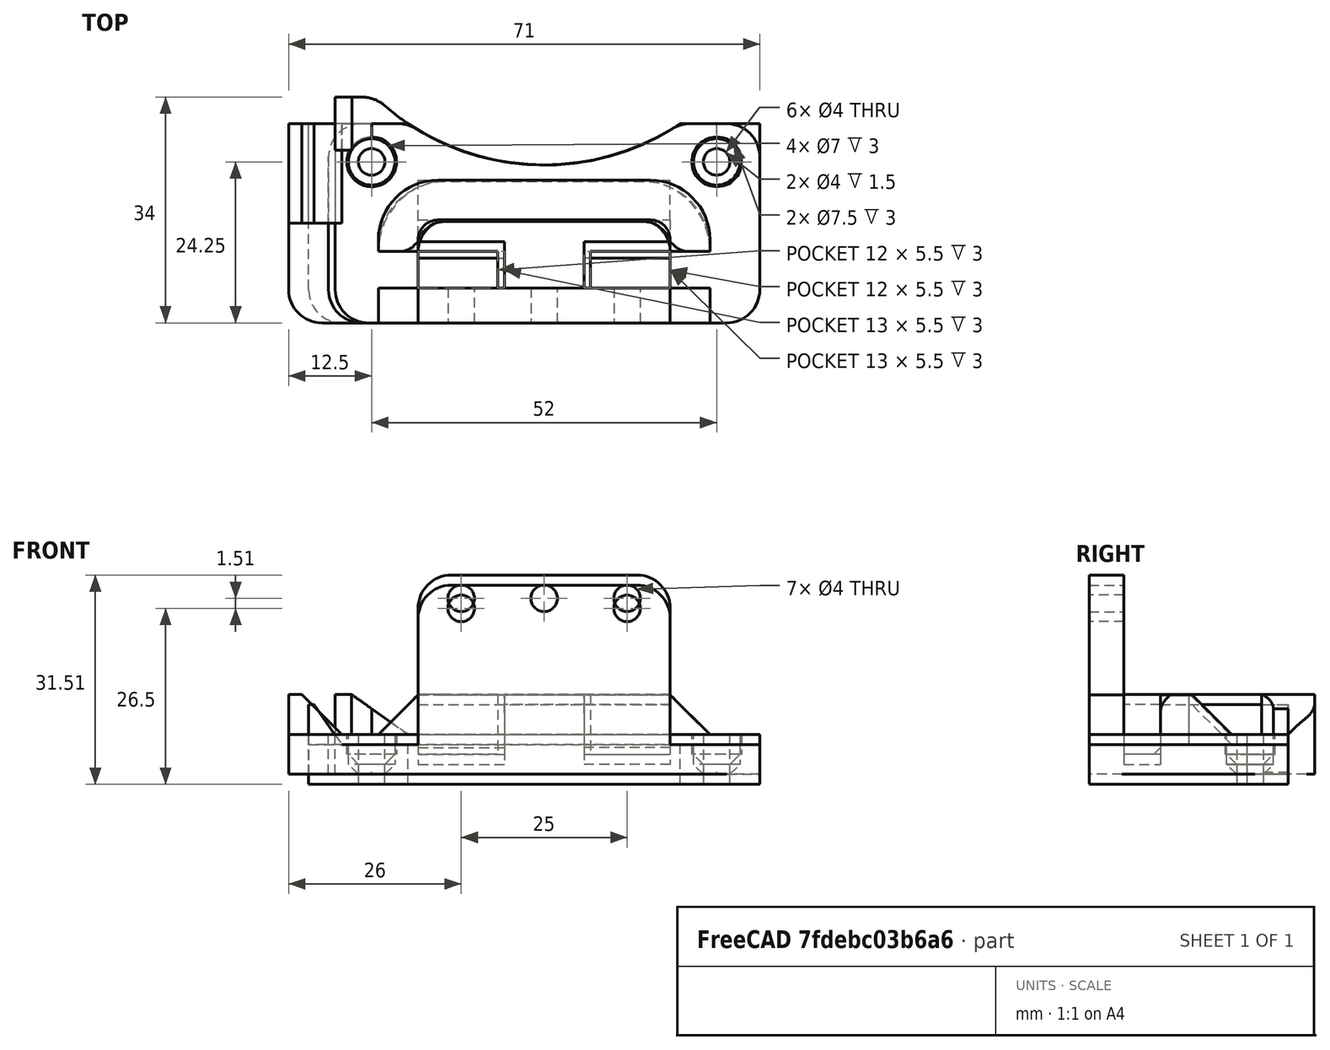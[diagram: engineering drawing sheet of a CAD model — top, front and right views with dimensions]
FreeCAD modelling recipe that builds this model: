
FCSTD DOCUMENT  (FreeCAD 0.18R4 (GitTag))
Label: y_belt_mount_v0.3
License: CreativeCommons Attribution-ShareAlike
LicenseURL: http://creativecommons.org/licenses/by-sa/4.0/
objects: Sketcher::SketchObject×7, PartDesign::Pocket×6, PartDesign::Fillet×3, PartDesign::Chamfer×3, Part::FeaturePython×2, App::FeaturePython×2, PartDesign::Pad×1, PartDesign::Body×1
note: 30 computed .brp shape members not serialized (recipe doc carries the construction recipe); baked Part::Feature solids carry a one-line shape summary decoded from their .brp

FEATURE [Sketcher::SketchObject] Sketch
  MapMode = 5
  Support = -> [XY_Plane]
  sketch-geometry (9):
    g0: LineSegment StartX=64 StartY=0 StartZ=0 EndX=64 EndY=30 EndZ=0
    g1: LineSegment StartX=64 StartY=30 StartZ=0 EndX=52 EndY=30 EndZ=0
    g2: LineSegment StartX=0 StartY=34 StartZ=0 EndX=0 EndY=0 EndZ=0
    g3: LineSegment StartX=0 StartY=0 StartZ=0 EndX=64 EndY=0 EndZ=0
    g4: ArcOfCircle CenterX=31.5 CenterY=60.5 CenterZ=0 NormalX=0 NormalY=0 NormalZ=1 AngleXU=0 Radius=36.7491 StartAngle=3.94699 EndAngle=5.30417
    g5: Circle CenterX=5.5 CenterY=24.25 CenterZ=0 NormalX=0 NormalY=0 NormalZ=1 AngleXU=0 Radius=2
    g6: Circle CenterX=57.5 CenterY=24.25 CenterZ=0 NormalX=0 NormalY=0 NormalZ=1 AngleXU=0 Radius=2
    g7: LineSegment [constr] StartX=5.5 StartY=24.25 StartZ=0 EndX=57.5 EndY=24.25 EndZ=0
    g8: LineSegment StartX=0 StartY=34 StartZ=0 EndX=6.03925 EndY=34 EndZ=0
  constraints (26):
    c: Coincident(g0,g1)
    c: Coincident(g2,g3)
    c: Coincident(g0,g3)
    c: Coincident(g2,g-1)
    c: Vertical(g2)
    c: Vertical(g0)
    c: Horizontal(g3)
    c: Horizontal(g1)
    c: DistanceX(g3,g3) = 64
    c: DistanceX(g1,g1) = 12
    c: Coincident(g1,g4)
    c: DistanceY(g0,g0) = 30
    c: DistanceX(g5) = 5.5
    c: DistanceY(g5) = 24.25
    c: Coincident(g6,g7)
    c: Coincident(g5,g7)
    c: Horizontal(g7)
    c: DistanceX(g7,g7) = 52
    c: Equal(g5,g6)
    c: Radius(g6) = 2
    c: DistanceX(g4) = 31.5
    c: DistanceY(g4) = 60.5
    c: DistanceY(g2,g2) = 34
    c: Horizontal(g8)
    c: Coincident(g4,g8)
    c: Coincident(g2,g8)
FEATURE [PartDesign::Pad] Pad
  Length = 30
  Length2 = 100
  Profile = -> Sketch
  Type = 0
FEATURE [Sketcher::SketchObject] Sketch001
  MapMode = 5
  Placement = pos=(0,0,30) rot=(0,0,1;0rad)
  Support = -> [Pad]
  sketch-geometry (10):
    g0: LineSegment StartX=5.5 StartY=30 StartZ=0 EndX=67 EndY=30 EndZ=0
    g1: LineSegment StartX=67 StartY=30 StartZ=0 EndX=67 EndY=0 EndZ=0
    g2: LineSegment StartX=67 StartY=0 StartZ=0 EndX=50.5 EndY=0 EndZ=0
    g3: LineSegment StartX=12.5 StartY=0 StartZ=0 EndX=0 EndY=0 EndZ=0
    g4: LineSegment StartX=5.5 StartY=30 StartZ=0 EndX=5.5 EndY=26 EndZ=0
    g5: LineSegment StartX=5.5 StartY=26 StartZ=0 EndX=0 EndY=26 EndZ=0
    g6: LineSegment StartX=0 StartY=26 StartZ=0 EndX=0 EndY=0 EndZ=0
    g7: LineSegment StartX=12.5 StartY=0 StartZ=0 EndX=12.5 EndY=15.5 EndZ=0
    g8: LineSegment StartX=12.5 StartY=15.5 StartZ=0 EndX=50.5 EndY=15.5 EndZ=0
    g9: LineSegment StartX=50.5 StartY=15.5 StartZ=0 EndX=50.5 EndY=0 EndZ=0
  constraints (29):
    c: Coincident(g0,g1)
    c: Coincident(g1,g2)
    c: Horizontal(g3)
    c: Horizontal(g2)
    c: Horizontal(g0)
    c: Vertical(g1)
    c: DistanceX(g0) = 67
    c: DistanceY(g0) = 30
    c: Coincident(g4,g5)
    c: Coincident(g5,g6)
    c: Coincident(g3,g6)
    c: Coincident(g3,g-1)
    c: Vertical(g6)
    c: Vertical(g4)
    c: Horizontal(g5)
    c: DistanceX(g5,g5) = 5.5
    c: Coincident(g0,g4)
    c: DistanceX(g3,g3) = 12.5
    c: PointOnObject(g1,g-1)
    c: DistanceX(g2,g2) = 16.5
    c: Coincident(g7,g8)
    c: Coincident(g8,g9)
    c: Coincident(g2,g9)
    c: Coincident(g3,g7)
    c: Vertical(g9)
    c: Vertical(g7)
    c: Horizontal(g8)
    c: DistanceY(g7,g7) = 15.5
    c: DistanceY(g4,g4) = 4
FEATURE [PartDesign::Pocket] Pocket
  BaseFeature = -> Pad
  Length = 24
  Length2 = 100
  Profile = -> Sketch001
  Type = 0
FEATURE [Sketcher::SketchObject] Sketch003
  MapMode = 5
  Placement = pos=(0,0,30) rot=(0,0,1;0rad)
  Support = -> [Pocket]
  sketch-geometry (4):
    g0: LineSegment StartX=9.5 StartY=21 StartZ=0 EndX=59.5 EndY=21 EndZ=0
    g1: LineSegment StartX=59.5 StartY=21 StartZ=0 EndX=59.5 EndY=5.25 EndZ=0
    g2: LineSegment StartX=59.5 StartY=5.25 StartZ=0 EndX=9.5 EndY=5.25 EndZ=0
    g3: LineSegment StartX=9.5 StartY=5.25 StartZ=0 EndX=9.5 EndY=21 EndZ=0
  constraints (12):
    c: Coincident(g0,g1)
    c: Coincident(g1,g2)
    c: Coincident(g2,g3)
    c: Coincident(g3,g0)
    c: Horizontal(g0)
    c: Horizontal(g2)
    c: Vertical(g1)
    c: Vertical(g3)
    c: DistanceX(g2) = 9.5
    c: DistanceY(g2) = 5.25
    c: DistanceY(g3,g3) = 15.75
    c: DistanceX(g0,g0) = 50
FEATURE [PartDesign::Pocket] Pocket001
  BaseFeature = -> Pocket
  Length = 18
  Length2 = 100
  Profile = -> Sketch003
  Type = 0
FEATURE [Sketcher::SketchObject] Sketch004
  MapMode = 5
  Placement = pos=(0,0,12) rot=(0,0,1;0rad)
  Support = -> [Pocket001]
  sketch-geometry (8):
    g0: LineSegment StartX=25.5 StartY=5.25 StartZ=0 EndX=12.5 EndY=5.25 EndZ=0
    g1: LineSegment StartX=12.5 StartY=5.25 StartZ=0 EndX=12.5 EndY=10.75 EndZ=0
    g2: LineSegment StartX=12.5 StartY=10.75 StartZ=0 EndX=25.5 EndY=10.75 EndZ=0
    g3: LineSegment StartX=25.5 StartY=10.75 StartZ=0 EndX=25.5 EndY=5.25 EndZ=0
    g4: LineSegment StartX=37.5 StartY=5.25 StartZ=0 EndX=50.5 EndY=5.25 EndZ=0
    g5: LineSegment StartX=50.5 StartY=5.25 StartZ=0 EndX=50.5 EndY=10.75 EndZ=0
    g6: LineSegment StartX=50.5 StartY=10.75 StartZ=0 EndX=37.5 EndY=10.75 EndZ=0
    g7: LineSegment StartX=37.5 StartY=10.75 StartZ=0 EndX=37.5 EndY=5.25 EndZ=0
  constraints (24):
    c: Coincident(g0,g1)
    c: Coincident(g1,g2)
    c: Coincident(g2,g3)
    c: Coincident(g3,g0)
    c: Horizontal(g0)
    c: Horizontal(g2)
    c: Vertical(g1)
    c: Vertical(g3)
    c: Coincident(g4,g5)
    c: Coincident(g5,g6)
    c: Coincident(g6,g7)
    c: Coincident(g7,g4)
    c: Horizontal(g4)
    c: Horizontal(g6)
    c: Vertical(g5)
    c: Vertical(g7)
    c: DistanceX(g0) = 12.5
    c: DistanceY(g0) = 5.25
    c: DistanceY(g1,g1) = 5.5
    c: DistanceX(g2,g2) = 13
    c: PointOnObject(g0,g4)
    c: DistanceX(g0,g4) = 12
    c: Equal(g7,g3)
    c: Equal(g6,g2)
FEATURE [PartDesign::Pocket] Pocket002
  BaseFeature = -> Pocket001
  Length = 9
  Length2 = 100
  Profile = -> Sketch004
  Type = 0
FEATURE [Sketcher::SketchObject] Sketch005
  MapMode = 5
  Placement = pos=(0,0,0) rot=(1,0,0;1.5708rad)
  Support = -> [Pocket002]
  sketch-geometry (4):
    g0: Circle [constr] CenterX=19 CenterY=26.5 CenterZ=0 NormalX=0 NormalY=0 NormalZ=1 AngleXU=0 Radius=2
    g1: LineSegment [constr] StartX=19 StartY=26.5 StartZ=0 EndX=44 EndY=26.5 EndZ=0
    g2: Circle [constr] CenterX=44 CenterY=26.5 CenterZ=0 NormalX=0 NormalY=0 NormalZ=1 AngleXU=0 Radius=2
    g3: Circle CenterX=31.5 CenterY=26.5 CenterZ=0 NormalX=0 NormalY=0 NormalZ=1 AngleXU=0 Radius=2
  constraints (11):
    c: DistanceX(g0) = 19
    c: DistanceY(g0) = 26.5
    c: Coincident(g0,g1)
    c: Horizontal(g1)
    c: Coincident(g1,g2)
    c: DistanceX(g1,g1) = 25
    c: Radius(g2) = 2
    c: Equal(g2,g0)
    c: DistanceX(g0,g3) = 12.5
    c: Equal(g3,g0)
    c: PointOnObject(g3,g1)
FEATURE [PartDesign::Pocket] Pocket003
  BaseFeature = -> Pocket002
  Length = 5
  Length2 = 100
  Profile = -> Sketch005
  Type = 1
FEATURE [Sketcher::SketchObject] Sketch006
  MapMode = 5
  Placement = pos=(0,0,30) rot=(0,0,1;0rad)
  Support = -> [Pocket003]
  sketch-geometry (2):
    g0: Circle CenterX=5.5 CenterY=24.25 CenterZ=0 NormalX=0 NormalY=0 NormalZ=1 AngleXU=0 Radius=3.5
    g1: Circle CenterX=57.5 CenterY=24.25 CenterZ=0 NormalX=0 NormalY=0 NormalZ=1 AngleXU=0 Radius=3.5
  constraints (6):
    c: DistanceX(g1) = 57.5
    c: DistanceY(g1) = 24.25
    c: Radius(g1) = 3.5
    c: DistanceX(g0,g1) = 52
    c: DistanceY(g0,g1) = 0
    c: Equal(g0,g1)
FEATURE [PartDesign::Pocket] Pocket004
  BaseFeature = -> Pocket003
  Length = 24
  Length2 = 100
  Profile = -> Sketch006
  Type = 0
FEATURE [Part::FeaturePython] b_y_belt_mount_001_  label="y_belt_mount_001"  # a2plus imported part (geometry in sourceFile) (typed FeaturePython)
  Placement = pos=(-7,0,0) rot=(0,0,1;0rad)
  a2p_Version = V0.1
  fixedPosition = true
  sourceFile = .\..\..\..\..\..\..\Desktop\printers\syn1\printed_parts\y_belt_mount\y_belt_mount.fcstd
  subassemblyImport = false
  timeLastImport = 1.57858e+09
  updateColors = true
FEATURE [Part::FeaturePython] b_y_belt_mount_001_001  label="y_belt_mount_002"  # a2plus imported part (geometry in sourceFile) (typed FeaturePython)
  Placement = pos=(-7,5.746e-12,-1.51) rot=(0,0,1;0rad)
  a2p_Version = V0.1
  fixedPosition = false
  sourceFile = .\..\..\..\..\..\..\Desktop\printers\syn1\printed_parts\y_belt_mount\y_belt_mount_v0..FCStd
  subassemblyImport = false
  timeLastImport = 1.58334e+09
  updateColors = true
FEATURE [App::FeaturePython] circularEdge_001  label="circularEdge_001__y_belt_mount_001"  # a2plus constraint (typed FeaturePython)
  Object1 = b_y_belt_mount_001_001
  Object2 = b_y_belt_mount_001_
  ParentTreeObject = -> b_y_belt_mount_001_001
  SubElement1 = Edge112
  SubElement2 = Edge39
  Type = circularEdge
  directionConstraint = 1
  lockRotation = false
  offset = 0
FEATURE [App::FeaturePython] circularEdge_001_mirror  label="circularEdge_001__y_belt_mount_002"  # a2plus constraint (typed FeaturePython)
  Object1 = b_y_belt_mount_001_001
  Object2 = b_y_belt_mount_001_
  ParentTreeObject = -> b_y_belt_mount_001_
  SubElement1 = Edge112
  SubElement2 = Edge39
  Type = circularEdge
  directionConstraint = 1
  lockRotation = false
  offset = 0
FEATURE [Sketcher::SketchObject] Sketch007
  MapMode = 5
  Placement = pos=(0,26,0) rot=(1,0,0;1.5708rad)
  Support = -> [Pocket004]
  sketch-geometry (5):
    g0: LineSegment StartX=0 StartY=12 StartZ=0 EndX=2.5 EndY=12 EndZ=0
    g1: LineSegment StartX=2.5 StartY=12 StartZ=0 EndX=11 EndY=6 EndZ=0
    g2: LineSegment StartX=11 StartY=6 StartZ=0 EndX=11 EndY=30 EndZ=0
    g3: LineSegment StartX=11 StartY=30 StartZ=0 EndX=0 EndY=30 EndZ=0
    g4: LineSegment StartX=0 StartY=30 StartZ=0 EndX=0 EndY=12 EndZ=0
  constraints (15):
    c: PointOnObject(g0,g-2)
    c: Horizontal(g0)
    c: Coincident(g0,g1)
    c: Coincident(g1,g2)
    c: Vertical(g2)
    c: Coincident(g2,g3)
    c: Horizontal(g3)
    c: Coincident(g3,g4)
    c: Coincident(g4,g0)
    c: Vertical(g4)
    c: DistanceY(g0) = 12
    c: DistanceY(g4,g4) = 18
    c: DistanceX(g3,g3) = 11
    c: DistanceX(g0,g0) = 2.5
    c: DistanceY(g2,g2) = 24
FEATURE [PartDesign::Pocket] Pocket005
  BaseFeature = -> Pocket004
  Length = 5
  Length2 = 100
  Profile = -> Sketch007
  Refine = true
  Type = 1
FEATURE [PartDesign::Fillet] Fillet
  Base = -> Pocket005 [Edge27,Edge31,Edge29,Edge41,Edge44,Edge14,Edge2]
  BaseFeature = -> Pocket005
  Radius = 5
FEATURE [PartDesign::Fillet] Fillet001
  Base = -> Fillet [Edge80,Edge83]
  BaseFeature = -> Fillet
  Radius = 3
FEATURE [PartDesign::Chamfer] Chamfer
  Base = -> Fillet001 [Edge8]
  BaseFeature = -> Fillet001
  Size = 5.99
FEATURE [PartDesign::Chamfer] Chamfer001
  Base = -> Chamfer [Edge33,Edge69]
  BaseFeature = -> Chamfer
  Size = 1.5
FEATURE [PartDesign::Fillet] Fillet002
  Base = -> Chamfer001 [Edge2,Edge87]
  BaseFeature = -> Chamfer001
  Radius = 3
FEATURE [PartDesign::Chamfer] Chamfer002
  Base = -> Fillet002 [Edge6,Edge86]
  BaseFeature = -> Fillet002
  Size = 1
FEATURE [PartDesign::Body] Body
  Group = -> [Sketch,Pad,Sketch001,Pocket,Sketch003,Pocket001,Sketch004,Pocket002,Sketch005,Pocket003,Sketch006,Pocket004,Sketch007,Pocket005,Fillet,Fillet001,Chamfer,Chamfer001,Fillet002,Chamfer002]
  Origin = -> Origin
  Tip = -> Chamfer002
